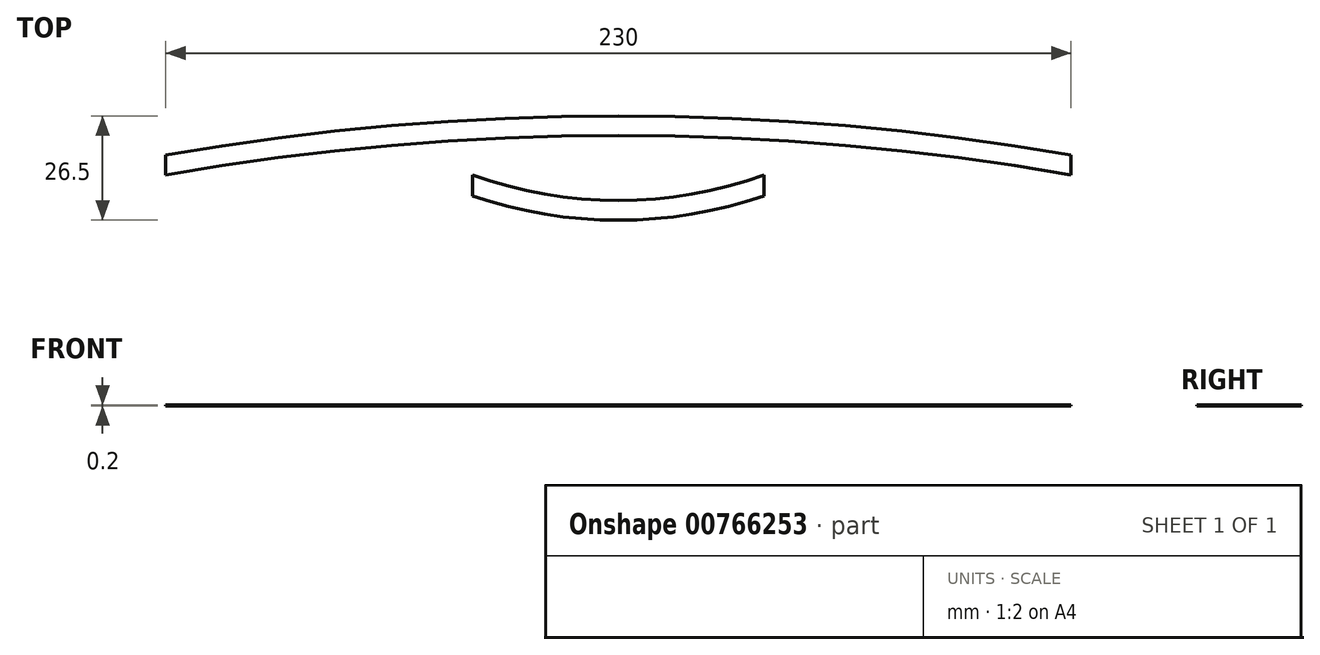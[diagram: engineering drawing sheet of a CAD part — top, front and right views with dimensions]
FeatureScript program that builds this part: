
annotation { "Feature Type Name" : "Feature", "Feature Type Description" : "" }
export const myFeature = defineFeature(function(context is Context, id is Id, definition is map)
    precondition{}
    {
        {
            var Q0;
            Q0=qCreatedBy(makeId("Top.planeOp"),FACE);
            var sketch = newSketch(context, id + "F0", { "sketchPlane" : qUnion([Q0])});
            skArc(sketch, "E0", {"start": v(115, 0) * mm, "mid": v(0, 10) * mm, "end": v(-115, 0) * mm});
            skArc(sketch, "E1.0", {"start": v(115, 5.08) * mm, "mid": v(0, 15) * mm, "end": v(-115, 5.08) * mm});
            skLineSegment(sketch, "E2", {"start": v(-115, 0) * mm, "end": v(-115, 5.08) * mm});
            skLineSegment(sketch, "E3", {"start": v(115, 0) * mm, "end": v(115, 5.08) * mm});
            skSolve(sketch);
        }
        {
            var Q0;
            Q0 = qSketchRegion(id + "F0", true);
            extrude(context, id + "F1", {"entities" : qUnion([Q0]), "depth" : 0.2 * mm, "offsetDistance" : 25 * mm});
        }
        {
            var Q0;
            Q0=qCreatedBy(makeId("Top.planeOp"),FACE);
            var sketch = newSketch(context, id + "F2", { "sketchPlane" : qUnion([Q0])});
            skArc(sketch, "E4", {"start": v(-37, 0) * mm, "mid": v(0, -6.5) * mm, "end": v(37, 0) * mm});
            skArc(sketch, "E5.0", {"start": v(-37, -5.3) * mm, "mid": v(0, -11.5) * mm, "end": v(37, -5.3) * mm});
            skLineSegment(sketch, "E6", {"start": v(-37, 0) * mm, "end": v(-37, -5.3) * mm});
            skLineSegment(sketch, "E7", {"start": v(37, 0) * mm, "end": v(37, -5.3) * mm});
            skSolve(sketch);
        }
        {
            var Q0;
            Q0 = qSketchRegion(id + "F2", true);
            extrude(context, id + "F3", {"entities" : qUnion([Q0]), "depth" : 0.2 * mm, "offsetDistance" : 25 * mm});
        }
    });
